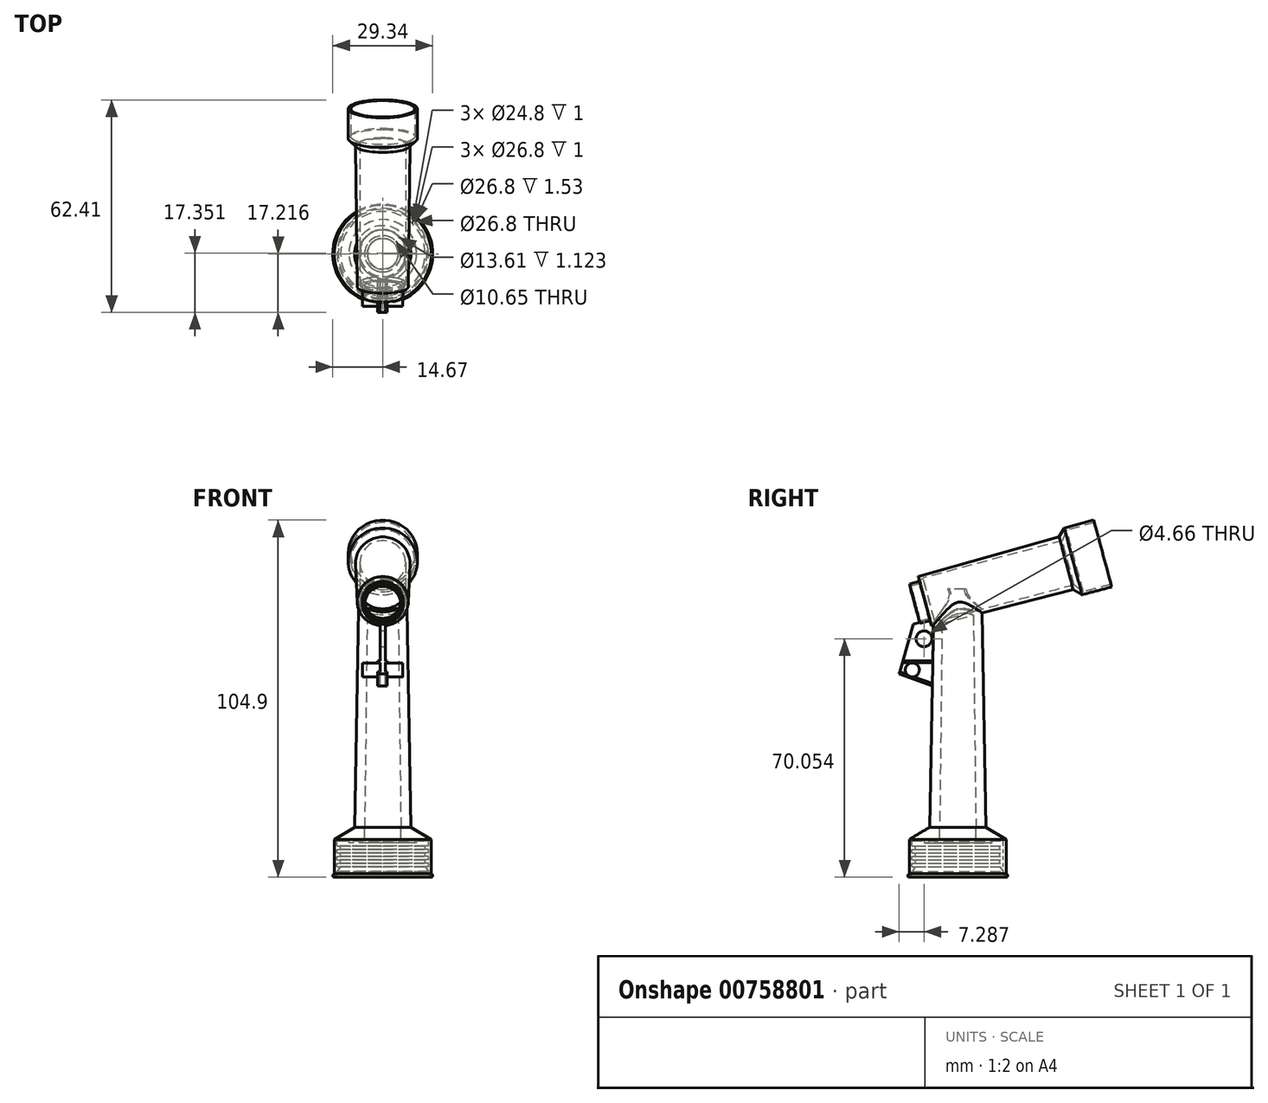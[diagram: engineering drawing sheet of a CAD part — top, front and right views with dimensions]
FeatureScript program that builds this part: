
annotation { "Feature Type Name" : "Feature", "Feature Type Description" : "" }
export const myFeature = defineFeature(function(context is Context, id is Id, definition is map)
    precondition{}
    {
        {
            var Q0;
            Q0=qCreatedBy(makeId("Right.planeOp"),FACE);
            var sketch = newSketch(context, id + "F0", { "sketchPlane" : qUnion([Q0])});
            skLineSegment(sketch, "E0", {"start": v(-40.8, 52.82) * mm, "end": v(-40.8, -26.68) * mm, "construction": true});
            skLineSegment(sketch, "E1", {"start": v(-32.55, -12.16) * mm, "end": v(-26.55, -15.77) * mm});
            skLineSegment(sketch, "E2", {"start": v(-26.55, -15.77) * mm, "end": v(-26.55, -25.77) * mm});
            skFitSpline(sketch, "E3", {"points": [v(-26.55, -25.77) * mm, v(-26.32, -25.98) * mm, v(-26.2, -26.25) * mm, v(-26.16, -26.63) * mm, v(-26.55, -26.88) * mm], "startDerivative": vector(1.13, -0.86) * mm, "endDerivative": vector(-1.81, -0.7) * mm});
            skLineSegment(sketch, "E4", {"start": v(-35.48, -12.16) * mm, "end": v(-35.48, -15.65) * mm});
            skLineSegment(sketch, "E5", {"start": v(-35.48, -15.65) * mm, "end": v(-35.48, -15.65) * mm});
            skLineSegment(sketch, "E6", {"start": v(-35.48, -15.65) * mm, "end": v(-27.76, -15.8) * mm});
            skLineSegment(sketch, "E7", {"start": v(-27.76, -15.8) * mm, "end": v(-27.4, -16.2) * mm});
            skLineSegment(sketch, "E8", {"start": v(-27.4, -16.2) * mm, "end": v(-27.4, -17.72) * mm});
            skLineSegment(sketch, "E9", {"start": v(-27.4, -17.72) * mm, "end": v(-28.4, -17.72) * mm});
            skLineSegment(sketch, "E10", {"start": v(-28.4, -17.72) * mm, "end": v(-28.4, -18.72) * mm});
            skLineSegment(sketch, "E11", {"start": v(-28.4, -18.72) * mm, "end": v(-27.4, -18.72) * mm});
            skLineSegment(sketch, "E12", {"start": v(-27.4, -18.72) * mm, "end": v(-27.4, -19.72) * mm});
            skLineSegment(sketch, "E13", {"start": v(-27.4, -19.72) * mm, "end": v(-28.4, -19.72) * mm});
            skLineSegment(sketch, "E14", {"start": v(-28.4, -19.72) * mm, "end": v(-28.4, -20.72) * mm});
            skLineSegment(sketch, "E15", {"start": v(-28.4, -20.72) * mm, "end": v(-27.4, -20.72) * mm});
            skLineSegment(sketch, "E16", {"start": v(-27.4, -20.72) * mm, "end": v(-27.4, -21.72) * mm});
            skLineSegment(sketch, "E17", {"start": v(-27.4, -21.72) * mm, "end": v(-28.4, -21.72) * mm});
            skLineSegment(sketch, "E18", {"start": v(-28.4, -21.72) * mm, "end": v(-28.4, -22.72) * mm});
            skLineSegment(sketch, "E19", {"start": v(-28.4, -22.72) * mm, "end": v(-27.4, -22.72) * mm});
            skLineSegment(sketch, "E20", {"start": v(-27.4, -22.72) * mm, "end": v(-27.4, -23.72) * mm});
            skLineSegment(sketch, "E21", {"start": v(-27.4, -23.72) * mm, "end": v(-28.4, -23.72) * mm});
            skLineSegment(sketch, "E22", {"start": v(-28.4, -23.72) * mm, "end": v(-27.4, -25.24) * mm});
            skLineSegment(sketch, "E23", {"start": v(-27.4, -25.24) * mm, "end": v(-27.4, -25.82) * mm});
            skLineSegment(sketch, "E24", {"start": v(-27.4, -25.82) * mm, "end": v(-26.55, -26.88) * mm});
            skLineSegment(sketch, "E25", {"start": v(-36.33, 57.72) * mm, "end": v(-33.8, 57.72) * mm});
            skLineSegment(sketch, "E26", {"start": v(-36.33, 57.72) * mm, "end": v(-35.48, -12.16) * mm});
            skLineSegment(sketch, "E27", {"start": v(-33.8, 57.72) * mm, "end": v(-32.55, -12.16) * mm});
            skSolve(sketch);
        }
        {
            var Q0;
            Q0=makeQuery(id+"F0.imprint","IMPRINT",FACE,{"disambiguationData":[TD([[makeQuery(id+"F0.imprint","IMPRINT",EDGE,{"derivedFrom":sQuery(id+"F0.wireOp",EDGE,"E1")}),-1.0]])]});
            var Q1;
            Q1=sQuery(id+"F0.wireOp",EDGE,"E0");
            revolve(context, id + "F1", {"surfaceOperationType" : NewSurfaceOperationType.NEW, "entities" : qUnion([Q0]), "axis" : qUnion([Q1]), "revolveType" : RevolveType.FULL});
        }
        {
            var Q0;
            Q0=qCreatedBy(makeId("Right.planeOp"),FACE);
            var sketch = newSketch(context, id + "F2", { "sketchPlane" : qUnion([Q0])});
            skLineSegment(sketch, "E28", {"start": v(-53.47, 53.42) * mm, "end": v(-0.34, 67.66) * mm, "construction": true});
            skLineSegment(sketch, "E29", {"start": v(-54.94, 59.24) * mm, "end": v(-52.04, 60.01) * mm});
            skLineSegment(sketch, "E30", {"start": v(-52.04, 60.01) * mm, "end": v(-52.43, 61.46) * mm});
            skLineSegment(sketch, "E31", {"start": v(-52.43, 61.46) * mm, "end": v(-11.03, 73.08) * mm});
            skLineSegment(sketch, "E32", {"start": v(-11.03, 73.08) * mm, "end": v(-9.56, 75.7) * mm});
            skLineSegment(sketch, "E33", {"start": v(-9.56, 75.7) * mm, "end": v(-0.86, 78.02) * mm});
            skLineSegment(sketch, "E34", {"start": v(-0.86, 78.02) * mm, "end": v(-0.67, 77.29) * mm});
            skLineSegment(sketch, "E35", {"start": v(-0.67, 77.29) * mm, "end": v(-8.79, 75.11) * mm});
            skLineSegment(sketch, "E36", {"start": v(-8.79, 75.11) * mm, "end": v(-10.1, 72) * mm});
            skLineSegment(sketch, "E37", {"start": v(-10.1, 72) * mm, "end": v(-50.99, 61.05) * mm});
            skLineSegment(sketch, "E38", {"start": v(-50.99, 61.05) * mm, "end": v(-50.63, 59.7) * mm});
            skLineSegment(sketch, "E39", {"start": v(-50.63, 59.7) * mm, "end": v(-54.86, 58.56) * mm});
            skLineSegment(sketch, "E40", {"start": v(-54.86, 58.56) * mm, "end": v(-54.94, 59.24) * mm});
            skSolve(sketch);
        }
        {
            var Q0;
            Q0=makeQuery(id+"F2.imprint","IMPRINT",FACE,{"disambiguationData":[TD([[makeQuery(id+"F2.imprint","IMPRINT",EDGE,{"derivedFrom":sQuery(id+"F2.wireOp",EDGE,"E29")}),-1.0]])]});
            var Q1;
            Q1=sQuery(id+"F2.wireOp",EDGE,"E28");
            revolve(context, id + "F3", {"operationType" : NewBodyOperationType.ADD, "surfaceOperationType" : NewSurfaceOperationType.NEW, "entities" : qUnion([Q0]), "axis" : qUnion([Q1]), "revolveType" : RevolveType.FULL});
        }
        {
            var Q0;
            Q0=qCreatedBy(makeId("Right.planeOp"),FACE);
            var sketch = newSketch(context, id + "F4", { "sketchPlane" : qUnion([Q0])});
            skLineSegment(sketch, "E41", {"start": v(-48.14, 31.33) * mm, "end": v(-48.03, 31.27) * mm});
            skLineSegment(sketch, "E42", {"start": v(-48.14, 29.23) * mm, "end": v(-48.03, 31.27) * mm});
            skLineSegment(sketch, "E43", {"start": v(-48.14, 29.23) * mm, "end": v(-58.02, 32.8) * mm});
            skLineSegment(sketch, "E44", {"start": v(-48.03, 31.27) * mm, "end": v(-47.6, 47.46) * mm});
            skLineSegment(sketch, "E45", {"start": v(-47.6, 47.46) * mm, "end": v(-48.37, 47.48) * mm});
            skLineSegment(sketch, "E46", {"start": v(-48.37, 47.48) * mm, "end": v(-48.8, 48.91) * mm});
            skLineSegment(sketch, "E47", {"start": v(-48.8, 48.91) * mm, "end": v(-51.8, 48.03) * mm});
            skLineSegment(sketch, "E48", {"start": v(-51.8, 48.03) * mm, "end": v(-53.85, 47.46) * mm});
            skLineSegment(sketch, "E49", {"start": v(-53.85, 47.46) * mm, "end": v(-58.02, 32.8) * mm});
            skSolve(sketch);
        }
        {
            var Q0;
            Q0=qSketchRegion(id+"F4",true);
            extrude(context, id + "F5", {"entities" : qUnion([Q0]), "operationType" : NewBodyOperationType.ADD, "depth" : 0.8 * mm, "offsetDistance" : 25 * mm});
        }
        {
            var Q0;
            Q0=qSketchRegion(id+"F4",true);
            extrude(context, id + "F6", {"entities" : qUnion([Q0]), "operationType" : NewBodyOperationType.ADD, "oppositeDirection" : true, "depth" : 0.8 * mm, "offsetDistance" : 25 * mm});
        }
        {
            var Q0;
            Q0=makeQuery(id+"F3.opRevolve","SWEPT_FACE",FACE,{"disambiguationData":[OSD([sQuery(id+"F2.wireOp",EDGE,"E36")])]});
            cPlane(context, id + "F7", {"entities" : qUnion([Q0]), "cplaneType" : CPlaneType.LINE_ANGLE, "offset" : 25 * mm, "angle" : 0 * degree, "width" : 150 * mm, "height" : 150 * mm});
        }
        {
            var Q0;
            Q0=qCreatedBy(id+"F7.planeOp",FACE);
            var sketch = newSketch(context, id + "F8", { "sketchPlane" : qUnion([Q0])});
            skLineSegment(sketch, "E50.bottom", {"start": v(-43.53, -40.48) * mm, "end": v(-6.05, -40.48) * mm});
            skLineSegment(sketch, "E50.top", {"start": v(-43.53, -67.46) * mm, "end": v(-6.05, -67.46) * mm});
            skLineSegment(sketch, "E50.left", {"start": v(-43.53, -40.48) * mm, "end": v(-43.53, -67.46) * mm});
            skLineSegment(sketch, "E50.right", {"start": v(-6.05, -40.48) * mm, "end": v(-6.05, -67.46) * mm});
            skSolve(sketch);
        }
        {
            var Q0;
            Q0=qSketchRegion(id+"F8",true);
            extrude(context, id + "F9", {"entities" : qUnion([Q0]), "depth" : 6 * mm, "offsetDistance" : 25 * mm});
        }
        {
            var Q0;
            Q0=makeQuery(id+"F9.opExtrude","SWEPT_BODY",BODY,{"disambiguationData":[OSD([sQuery(id+"F8.wireOp",EDGE,"E50.bottom"),sQuery(id+"F8.wireOp",EDGE,"E50.top"),sQuery(id+"F8.wireOp",EDGE,"E50.left"),sQuery(id+"F8.wireOp",EDGE,"E50.right")])]});
            var Q1;
            Q1=makeQuery(id+"F9.opExtrude","CAP_EDGE",EDGE,{"disambiguationData":[OSD([sQuery(id+"F8.wireOp",EDGE,"E50.top")])],"isStart":false});
            transform(context, id + "F10", {"entities" : qUnion([Q0]), "transformType" : TransformType.ROTATION, "transformAxis" : qUnion([Q1]), "angle" : 90 * degree, "makeCopy" : false});
        }
        {
            var Q0;
            Q0=makeQuery(id+"F9.opExtrude","CAP_FACE",FACE,{"disambiguationData":[OSD([sQuery(id+"F8.wireOp",EDGE,"E50.bottom"),sQuery(id+"F8.wireOp",EDGE,"E50.top"),sQuery(id+"F8.wireOp",EDGE,"E50.left"),sQuery(id+"F8.wireOp",EDGE,"E50.right")])],"isStart":false});
            cPlane(context, id + "F11", {"entities" : qUnion([Q0]), "cplaneType" : CPlaneType.OFFSET, "offset" : 49 * mm, "oppositeDirection" : true, "width" : 150 * mm, "height" : 150 * mm});
        }
        {
            var Q0;
            Q0=makeQuery(id+"F9.opExtrude","SWEPT_BODY",BODY,{"disambiguationData":[OSD([sQuery(id+"F8.wireOp",EDGE,"E50.bottom"),sQuery(id+"F8.wireOp",EDGE,"E50.top"),sQuery(id+"F8.wireOp",EDGE,"E50.left"),sQuery(id+"F8.wireOp",EDGE,"E50.right")])]});
            transform(context, id + "F12", {"entities" : qUnion([Q0]), "transformType" : TransformType.TRANSLATION_3D, "dx" : -184 * mm, "dy" : 0 * mm, "dz" : 0 * mm, "makeCopy" : false});
        }
        {
            var Q0;
            Q0=qCreatedBy(makeId("Top.planeOp"),FACE);
            cPlane(context, id + "F13", {"entities" : qUnion([Q0]), "cplaneType" : CPlaneType.OFFSET, "offset" : 13.3 * mm, "oppositeDirection" : true, "width" : 150 * mm, "height" : 150 * mm});
        }
        {
            var Q0;
            Q0=qCreatedBy(id+"F13.planeOp",FACE);
            var sketch = newSketch(context, id + "F14", { "sketchPlane" : qUnion([Q0])});
            skCircle(sketch, "E51", {"center": v(0, -40.67) * mm, "radius": 6.8 * mm});
            skCircle(sketch, "E52", {"center": v(0, -40.67) * mm, "radius": 9.94 * mm});
            skSolve(sketch);
        }
        {
            var Q0;
            Q0=qSketchRegion(id+"F14",true);
            extrude(context, id + "F15", {"entities" : qUnion([Q0]), "operationType" : NewBodyOperationType.ADD, "oppositeDirection" : true, "depth" : 3.5 * mm, "offsetDistance" : 25 * mm});
        }
        {
            var Q0;
            Q0=qCreatedBy(id+"F11.planeOp",FACE);
            cPlane(context, id + "F16", {"entities" : qUnion([Q0]), "cplaneType" : CPlaneType.OFFSET, "offset" : 55 * mm, "oppositeDirection" : true, "width" : 150 * mm, "height" : 150 * mm});
        }
        {
            var Q0;
            Q0=qCreatedBy(makeId("Front.planeOp"),FACE);
            var sketch = newSketch(context, id + "F17", { "sketchPlane" : qUnion([Q0])});
            skLineSegment(sketch, "E53.bottom", {"start": v(-75.54, 62.8) * mm, "end": v(-43.91, 62.8) * mm});
            skLineSegment(sketch, "E53.top", {"start": v(-75.54, 28.7) * mm, "end": v(-43.91, 28.7) * mm});
            skLineSegment(sketch, "E53.left", {"start": v(-75.54, 62.8) * mm, "end": v(-75.54, 28.7) * mm});
            skLineSegment(sketch, "E53.right", {"start": v(-43.91, 62.8) * mm, "end": v(-43.91, 28.7) * mm});
            skSolve(sketch);
        }
        {
            var Q0;
            Q0=makeQuery(id+"F17.imprint","IMPRINT",FACE,{"disambiguationData":[TD([[makeQuery(id+"F17.imprint","IMPRINT",EDGE,{"derivedFrom":sQuery(id+"F17.wireOp",EDGE,"E53.bottom")}),-1.0]])]});
            extrude(context, id + "F18", {"entities" : qUnion([Q0]), "depth" : 5 * mm, "offsetDistance" : 25 * mm});
        }
        {
            var Q0;
            Q0=makeQuery(id+"F18.opExtrude","SWEPT_BODY",BODY,{"disambiguationData":[OSD([sQuery(id+"F17.wireOp",EDGE,"E53.bottom"),sQuery(id+"F17.wireOp",EDGE,"E53.top"),sQuery(id+"F17.wireOp",EDGE,"E53.left"),sQuery(id+"F17.wireOp",EDGE,"E53.right")])]});
            var Q1;
            Q1=makeQuery(id+"F18.opExtrude","CAP_EDGE",EDGE,{"disambiguationData":[OSD([sQuery(id+"F17.wireOp",EDGE,"E53.bottom")])],"isStart":true});
            transform(context, id + "F19", {"entities" : qUnion([Q0]), "transformType" : TransformType.ROTATION, "transformAxis" : qUnion([Q1]), "angle" : 15 * degree, "oppositeDirection" : true, "makeCopy" : false});
        }
        {
            var Q0;
            Q0=makeQuery(id+"F18.opExtrude","SWEPT_BODY",BODY,{"disambiguationData":[OSD([sQuery(id+"F17.wireOp",EDGE,"E53.bottom"),sQuery(id+"F17.wireOp",EDGE,"E53.top"),sQuery(id+"F17.wireOp",EDGE,"E53.left"),sQuery(id+"F17.wireOp",EDGE,"E53.right")])]});
            transform(context, id + "F20", {"entities" : qUnion([Q0]), "transformType" : TransformType.TRANSLATION_3D, "dx" : -200.4 * mm, "dy" : 0 * mm, "dz" : 0 * mm, "makeCopy" : false});
        }
        {
            var Q0;
            Q0=makeQuery(id+"F18.opExtrude","SWEPT_BODY",BODY,{"disambiguationData":[OSD([sQuery(id+"F17.wireOp",EDGE,"E53.bottom"),sQuery(id+"F17.wireOp",EDGE,"E53.top"),sQuery(id+"F17.wireOp",EDGE,"E53.left"),sQuery(id+"F17.wireOp",EDGE,"E53.right")])]});
            var Q1;
            Q1=makeQuery(id+"F9.opExtrude","SWEPT_BODY",BODY,{"disambiguationData":[OSD([sQuery(id+"F8.wireOp",EDGE,"E50.bottom"),sQuery(id+"F8.wireOp",EDGE,"E50.top"),sQuery(id+"F8.wireOp",EDGE,"E50.left"),sQuery(id+"F8.wireOp",EDGE,"E50.right")])]});
            deleteBodies(context, id + "F21", {"entities" : qUnion([Q0, Q1])});
        }
        {
            var Q0;
            Q0=makeQuery(id+"F5.opExtrude","CAP_FACE",FACE,{"disambiguationData":[OSD([sQuery(id+"F4.wireOp",EDGE,"E42"),sQuery(id+"F4.wireOp",EDGE,"E43"),sQuery(id+"F4.wireOp",EDGE,"E44"),sQuery(id+"F4.wireOp",EDGE,"E45"),sQuery(id+"F4.wireOp",EDGE,"E46"),sQuery(id+"F4.wireOp",EDGE,"E47"),sQuery(id+"F4.wireOp",EDGE,"E48"),sQuery(id+"F4.wireOp",EDGE,"E49")])],"isStart":false});
            var sketch = newSketch(context, id + "F22", { "sketchPlane" : qUnion([Q0])});
            skLineSegment(sketch, "E54", {"start": v(-48.14, 36.7) * mm, "end": v(-56.9, 36.7) * mm});
            skLineSegment(sketch, "E55", {"start": v(-57.08, 36.1) * mm, "end": v(-48.15, 36.1) * mm});
            skLineSegment(sketch, "E56", {"start": v(-48.14, 36.7) * mm, "end": v(-48.15, 36.1) * mm});
            skLineSegment(sketch, "E57", {"start": v(-57.08, 36.1) * mm, "end": v(-56.9, 36.7) * mm});
            skLineSegment(sketch, "E58", {"start": v(-48.26, 30.12) * mm, "end": v(-57.84, 33.44) * mm});
            skLineSegment(sketch, "E59", {"start": v(-57.84, 33.44) * mm, "end": v(-58.02, 32.8) * mm});
            skLineSegment(sketch, "E60", {"start": v(-58.02, 32.8) * mm, "end": v(-48.27, 29.28) * mm});
            skLineSegment(sketch, "E61", {"start": v(-48.27, 29.28) * mm, "end": v(-48.26, 30.12) * mm});
            skSolve(sketch);
        }
        {
            var Q0;
            Q0=makeQuery(id+"F22.imprint","IMPRINT",FACE,{"disambiguationData":[TD([[makeQuery(id+"F22.imprint","IMPRINT",EDGE,{"derivedFrom":sQuery(id+"F22.wireOp",EDGE,"E54")}),1.0]])]});
            var Q1;
            Q1=makeQuery(id+"F22.imprint","IMPRINT",FACE,{"disambiguationData":[TD([[makeQuery(id+"F22.imprint","IMPRINT",EDGE,{"derivedFrom":sQuery(id+"F22.wireOp",EDGE,"E58")}),1.0]])]});
            extrude(context, id + "F23", {"entities" : qUnion([Q0, Q1]), "operationType" : NewBodyOperationType.ADD, "depth" : 0.5 * mm, "offsetDistance" : 25 * mm});
        }
        {
            var Q0;
            Q0=makeQuery(id+"F23.opExtrude","CAP_FACE",FACE,{"disambiguationData":[OSD([sQuery(id+"F22.wireOp",EDGE,"E54"),sQuery(id+"F22.wireOp",EDGE,"E55"),sQuery(id+"F22.wireOp",EDGE,"E56"),sQuery(id+"F22.wireOp",EDGE,"E57")])],"isStart":false});
            var Q1;
            Q1=makeQuery(id+"F23.opExtrude","CAP_FACE",FACE,{"disambiguationData":[OSD([sQuery(id+"F22.wireOp",EDGE,"E58"),sQuery(id+"F22.wireOp",EDGE,"E59"),sQuery(id+"F22.wireOp",EDGE,"E60"),sQuery(id+"F22.wireOp",EDGE,"E61")])],"isStart":false});
            extrude(context, id + "F24", {"entities" : qUnion([Q0, Q1]), "operationType" : NewBodyOperationType.ADD, "oppositeDirection" : true, "depth" : 2.8 * mm, "offsetDistance" : 25 * mm});
        }
        {
            var Q0;
            {var subQ0=sQuery(id+"F4.wireOp",EDGE,"E48");var subQ1=sQuery(id+"F4.wireOp",EDGE,"E49");Q0=makeQuery(id+"F23.boolean.opBoolean","SPLIT",FACE,{"disambiguationData":[TD([makeQuery(id+"F3.opRevolve","SWEPT_FACE",FACE,{"disambiguationData":[OSD([sQuery(id+"F2.wireOp",EDGE,"E29")])]})])],"derivedFrom":makeQuery(id+"F5.opExtrude","CAP_FACE",FACE,{"disambiguationData":[OSD([sQuery(id+"F4.wireOp",EDGE,"E42"),sQuery(id+"F4.wireOp",EDGE,"E43"),sQuery(id+"F4.wireOp",EDGE,"E44"),sQuery(id+"F4.wireOp",EDGE,"E45"),sQuery(id+"F4.wireOp",EDGE,"E46"),sQuery(id+"F4.wireOp",EDGE,"E47"),subQ0,subQ1])],"isStart":false})});}
            var sketch = newSketch(context, id + "F25", { "sketchPlane" : qUnion([Q0])});
            skCircle(sketch, "E62", {"center": v(-54.17, 34.02) * mm, "radius": 2.06 * mm});
            skCircle(sketch, "E63", {"center": v(-50.73, 43.17) * mm, "radius": 2.33 * mm});
            skSolve(sketch);
        }
        {
            var Q0;
            Q0=makeQuery(id+"F25.imprint","IMPRINT",FACE,{"disambiguationData":[TD([[makeQuery(id+"F25.imprint","IMPRINT",EDGE,{"derivedFrom":sQuery(id+"F25.wireOp",EDGE,"E63")}),1.0]])]});
            extrude(context, id + "F26", {"entities" : qUnion([Q0]), "operationType" : NewBodyOperationType.REMOVE, "oppositeDirection" : true, "depth" : 25 * mm, "offsetDistance" : 25 * mm});
        }
        {
            var Q0;
            Q0=makeQuery(id+"F25.imprint","IMPRINT",FACE,{"disambiguationData":[TD([[makeQuery(id+"F25.imprint","IMPRINT",EDGE,{"derivedFrom":sQuery(id+"F25.wireOp",EDGE,"E62")}),1.0]])]});
            extrude(context, id + "F27", {"entities" : qUnion([Q0]), "operationType" : NewBodyOperationType.ADD, "depth" : 5 * mm, "offsetDistance" : 25 * mm});
        }
        {
            var Q0;
            Q0=makeQuery(id+"F27.opExtrude","CAP_FACE",FACE,{"disambiguationData":[OSD([sQuery(id+"F25.wireOp",EDGE,"E62")])],"isStart":false});
            extrude(context, id + "F28", {"entities" : qUnion([Q0]), "operationType" : NewBodyOperationType.ADD, "oppositeDirection" : true, "depth" : 11.8 * mm, "offsetDistance" : 25 * mm});
        }
        {
            var Q0;
            Q0=makeQuery(id+"F3.opRevolve","SWEPT_FACE",FACE,{"disambiguationData":[OSD([sQuery(id+"F2.wireOp",EDGE,"E34")])]});
            var sketch = newSketch(context, id + "F29", { "sketchPlane" : qUnion([Q0])});
            skCircle(sketch, "E64", {"center": v(0, 65.44) * mm, "radius": 5.14 * mm});
            skSolve(sketch);
        }
        {
            var Q0;
            Q0=makeQuery(id+"F29.imprint","IMPRINT",FACE,{"disambiguationData":[TD([[makeQuery(id+"F29.imprint","IMPRINT",EDGE,{"derivedFrom":sQuery(id+"F29.wireOp",EDGE,"E64")}),1.0]])]});
            extrude(context, id + "F30", {"entities" : qUnion([Q0]), "operationType" : NewBodyOperationType.REMOVE, "oppositeDirection" : true, "depth" : 100 * mm, "offsetDistance" : 25 * mm});
        }
        {
            var Q0;
            Q0=makeQuery(id+"F3.opRevolve","SWEPT_FACE",FACE,{"disambiguationData":[OSD([sQuery(id+"F2.wireOp",EDGE,"E34")])]});
            var sketch = newSketch(context, id + "F31", { "sketchPlane" : qUnion([Q0])});
            skCircle(sketch, "E65", {"center": v(0, 65.44) * mm, "radius": 6.55 * mm});
            skSolve(sketch);
        }
        {
            var Q0;
            Q0=makeQuery(id+"F31.imprint","IMPRINT",FACE,{"disambiguationData":[TD([[makeQuery(id+"F31.imprint","IMPRINT",EDGE,{"derivedFrom":sQuery(id+"F31.wireOp",EDGE,"E65")}),1.0]])]});
            extrude(context, id + "F32", {"entities" : qUnion([Q0]), "operationType" : NewBodyOperationType.REMOVE, "oppositeDirection" : true, "depth" : 53.8 * mm, "offsetDistance" : 25 * mm});
        }
    });
